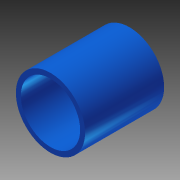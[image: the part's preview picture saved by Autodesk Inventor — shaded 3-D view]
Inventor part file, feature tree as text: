
AUTODESK INVENTOR PART (.ipt)
format: ipt  version: 2012 (Build 160160000, 160)  size: 82,432 bytes
history: native  units: in
note: dims shown in document units (in); Inventor stores cm internally (conversion verified against a paired STEP export)
features: other x3, sketch x1
ambient origin geometry x8: Origin, YZ Plane, XZ Plane, XY Plane, X Axis, Y Axis, Z Axis, Center Point
bodies: Solid1 (feature_tree)
feature tree (4):
  other  "WheelTread.ipt"
  other  "Solid1::WheelTread.ipt"
  sketch  "Sketch1"  dims[d0=0.3937in]
  other  "TaggingFeature1"
